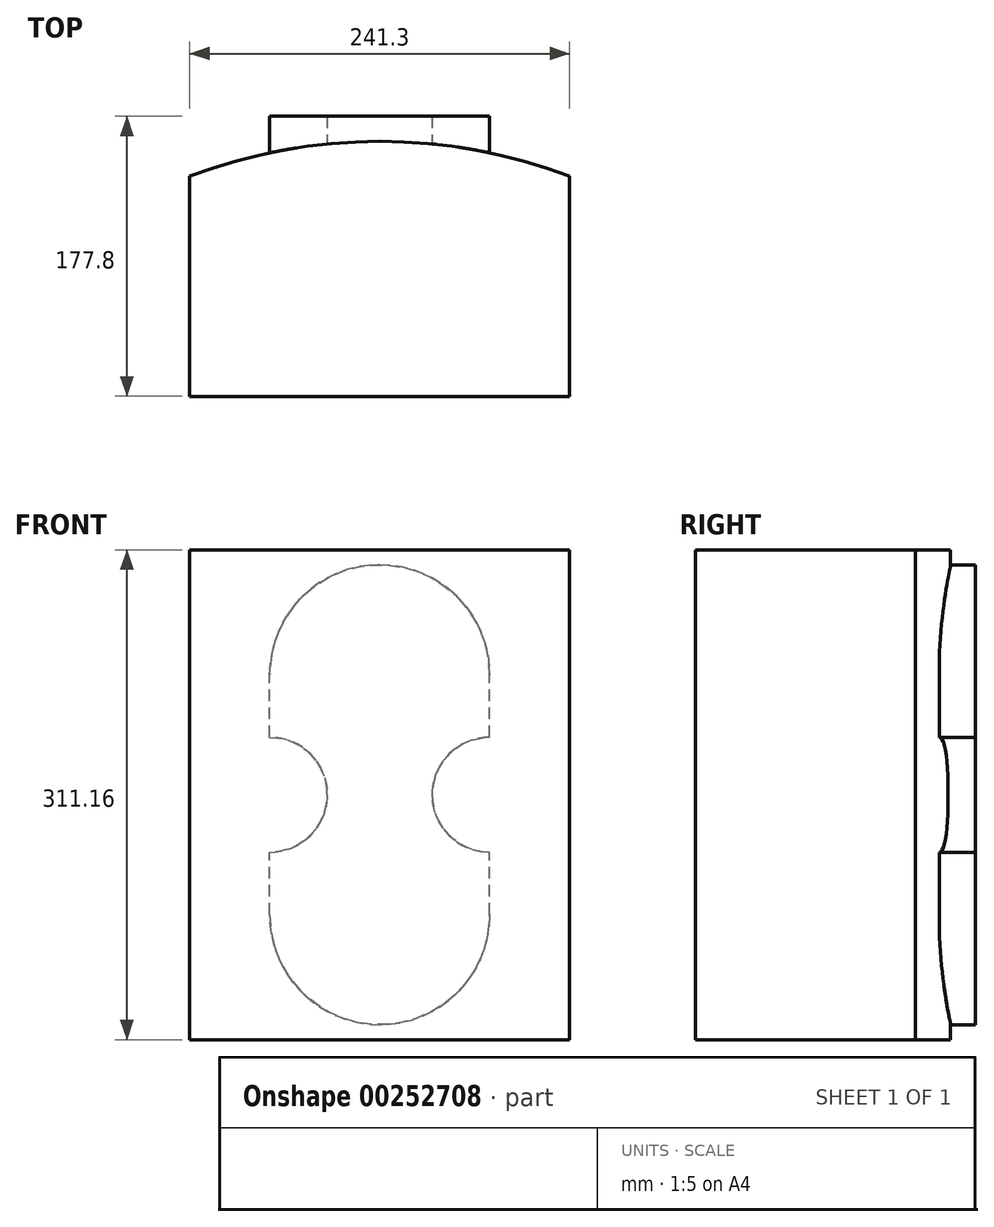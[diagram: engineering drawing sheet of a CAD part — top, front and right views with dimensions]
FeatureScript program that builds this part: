
annotation { "Feature Type Name" : "Feature", "Feature Type Description" : "" }
export const myFeature = defineFeature(function(context is Context, id is Id, definition is map)
    precondition{}
    {
        {
            var Q0;
            Q0=qCreatedBy(makeId("Front.planeOp"),FACE);
            var sketch = newSketch(context, id + "F0", { "sketchPlane" : qUnion([Q0])});
            skLineSegment(sketch, "E0.bottom", {"start": v(120.65, -155.58) * mm, "end": v(-120.65, -155.58) * mm});
            skLineSegment(sketch, "E0.top", {"start": v(120.65, 155.58) * mm, "end": v(-120.65, 155.57) * mm});
            skLineSegment(sketch, "E0.left", {"start": v(120.65, -155.58) * mm, "end": v(120.65, 155.58) * mm});
            skLineSegment(sketch, "E0.right", {"start": v(-120.65, -155.58) * mm, "end": v(-120.65, 155.57) * mm});
            skPoint(sketch, "E0.middle", {"position": v(0, 0) * mm});
            skSolve(sketch);
        }
        {
            var Q0;
            Q0 = qSketchRegion(id + "F0", true);
            extrude(context, id + "F1", {"entities" : qUnion([Q0]), "depth" : 127 * mm + 1 / 203.2 * mm});
        }
        {
            var Q0;
            Q0=makeQuery(id+"F1.opExtrude","SWEPT_FACE",FACE,{"disambiguationData":[OSD([sQuery(id+"F0.wireOp",EDGE,"E0.top")])]});
            var sketch = newSketch(context, id + "F2", { "sketchPlane" : qUnion([Q0])});
            skLineSegment(sketch, "E1", {"start": v(-120.65, 0) * mm, "end": v(-120.65, 12.7) * mm});
            skLineSegment(sketch, "E2", {"start": v(120.65, 0) * mm, "end": v(120.65, 12.7) * mm});
            skArc(sketch, "E3", {"start": v(120.65, 12.7) * mm, "mid": v(0, 34.93) * mm, "end": v(-120.65, 12.7) * mm});
            skSolve(sketch);
        }
        {
            var Q0;
            Q0=makeQuery(id+"F2.imprint","IMPRINT",FACE,{"disambiguationData":[TD([[makeQuery(id+"F2.imprint","IMPRINT",EDGE,{"derivedFrom":sQuery(id+"F2.wireOp",EDGE,"E1")}),-1.0]])]});
            var Q1;
            Q1=makeQuery(id+"F1.opExtrude","SWEPT_FACE",FACE,{"disambiguationData":[OSD([sQuery(id+"F0.wireOp",EDGE,"E0.bottom")])]});
            extrude(context, id + "F3", {"entities" : qUnion([Q0]), "operationType" : NewBodyOperationType.ADD, "endBound" : BoundingType.UP_TO_SURFACE, "oppositeDirection" : true, "endBoundEntityFace" : qUnion([Q1]), "depth" : 25.4 * mm});
        }
        {
            var Q0;
            Q0=qCreatedBy(makeId("Front.planeOp"),FACE);
            var sketch = newSketch(context, id + "F4", { "sketchPlane" : qUnion([Q0])});
            skArc(sketch, "E4", {"start": v(69.85, 76.2) * mm, "mid": v(0, 146.05) * mm, "end": v(-69.85, 76.2) * mm});
            skArc(sketch, "E5", {"start": v(-69.85, -76.2) * mm, "mid": v(0, -146.05) * mm, "end": v(69.85, -76.2) * mm});
            skArc(sketch, "E6", {"start": v(69.85, 36.51) * mm, "mid": v(33.34, 0) * mm, "end": v(69.85, -36.51) * mm});
            skLineSegment(sketch, "E7", {"start": v(69.85, 36.51) * mm, "end": v(69.85, 76.2) * mm});
            skLineSegment(sketch, "E8", {"start": v(69.85, -36.51) * mm, "end": v(69.85, -76.2) * mm});
            skLineSegment(sketch, "E9", {"start": v(0, 76.2) * mm, "end": v(0, -76.2) * mm, "construction": true});
            skLineSegment(sketch, "E10.MirrorCS", {"start": v(-69.85, -36.51) * mm, "end": v(-69.85, -76.2) * mm});
            skArc(sketch, "E11.MirrorCS", {"start": v(-69.85, 36.51) * mm, "mid": v(-33.34, 0) * mm, "end": v(-69.85, -36.51) * mm});
            skLineSegment(sketch, "E12.MirrorCS", {"start": v(-69.85, 36.51) * mm, "end": v(-69.85, 76.2) * mm});
            skSolve(sketch);
        }
        {
            var Q0;
            Q0 = qSketchRegion(id + "F4", true);
            extrude(context, id + "F5", {"entities" : qUnion([Q0]), "operationType" : NewBodyOperationType.ADD, "oppositeDirection" : true, "depth" : 50.8 * mm});
        }
    });
